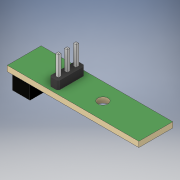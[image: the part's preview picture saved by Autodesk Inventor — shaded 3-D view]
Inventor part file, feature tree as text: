
AUTODESK INVENTOR PART (.ipt)
format: ipt  version: 2019 (Build 230136000, 136)  size: 507,904 bytes
history: native  units: mm
features: extrude x5, sketch x5, other x4, chamfer x2, projected_geometry x2
ambient origin geometry x8: Origin, YZ Plane, XZ Plane, XY Plane, X Axis, Y Axis, Z Axis, Center Point
bodies: Body1 (feature_tree)
feature tree (18):
  other  "Твердое тело1"
  extrude  "Выдавливание1"  Depth=10.0mm
  extrude  "Выдавливание2"  Depth=15.6mm
  chamfer  "Фаска1"  Distance=3.0mm
  extrude  "Выдавливание3"  Depth=1.6mm TaperAngle=0.0deg
  chamfer  "Фаска2"  Distance=2.6mm
  sketch  "Эскиз5"
  extrude  "Выдавливание4"  Depth=8.0mm
  extrude  "Выдавливание5"  Depth=10.9mm
  sketch  "Эскиз2"
  other  "Картинка1"
  sketch  "Эскиз3"
  other  "Картинка2"
  sketch  "Эскиз4"
  projected_geometry  "Спроецированная петля1"
  other  "Картинка3"
  sketch  "Эскиз6"
  projected_geometry  "Спроецированная петля2"
